# Revit family: VLGFP1002-xxxWSxxxBxxx
name_source: partatom
category: Oprawy oświetleniowe
revit_build: Autodesk Revit 2017 (Build: 20190508_0315(x64)
units: mm (PartAtom-declared; Revit-internal decimal feet)

## family parameters
Numer OmniClass = 23.80.70.11
Obiekt nadrzędny = Powierzchnia
Punkt obliczania pomieszczeń = Nie
Tnij formami wycięć po wczytaniu = Nie
Typ części = Normalny
Tytuł OmniClass = Luminaries for Internal Lighting
Współdzielony = Nie
Wymiar okrągłego złącza = Użyj średnicy
Źródło światła = Tak

## types (16) — shared parameters
Emituj kształt widoczny w renderingu = Nie
Emituj z długości prostokąta = 63 mm  [stored 0.206693 ft]
Emituj z szerokości prostokąta = 969 mm
Filtr koloru = 16777215
Kod zespołu = D5020200
Lampa = LED
Odchylenie kierunku = 90.00°
Plik sieci fotometrycznej = VLGFP1501-5NDWS840B0800.IES
Producent = RIDI Leuchten GmbH
URL = www.ridi.de
Zmiana temperatury barwowej przyciemniania lampy = <Brak>
brand = RIDI
conformity mark = CE
electrical safety class = 1
height = 66 mm  [stored 0.216535 ft]
ingress protection (IP) code = IP54
length = 1000 mm  [stored 3.28084 ft]
nominal frequency = 50-60Hz
nominal voltage = 230
voltage type (AC, DC, UC) = AC
weight = 1.64 kg
width = 67 mm
zero-valued in all types: Domyślna rzędna

## per-type parameters (varying)
| type | Model | Obciążenie pozorne | product name | rated input power |
| VLGFP1002-5NDWS830B0950 | 1551033 | 66 VA | VLGFP1002-5NDWS830B0950 | 66 |
| VLGFP1002-7DAWS830B0950 | 1561033
1561033
1561033 | 66 VA | VLGFP1002-7DAWS830B0950 | 66 |
| VLGFP1002-5NDWS830B1100 | 1551093 | 81 VA | VLGFP1002-5NDWS830B1100 | 81 |
| VLGFP1002-7DAWS830B1100 | 1561093 | 81 VA | VLGFP1002-5NDWS830B1100 | 81 |
| VLGFP1002-5NDWS840B1000 | 1551013 | 66 VA | VLGFP1002-5NDWS830B1100 | 66 |
| VLGFP1002-7DAWS840B1000 | 1561013 | 66 VA | VLGFP1002-7DAWS840B1000 | 66 |
| VLGFP1002-5NDWS840B1200 | 1551089 | 81 VA | VLGFP1002-5NDWS840B1200 | 81 |
| VLGFP1002-7NDWS840B1200 | 1561089 | 81 VA | VLGFP1002-7NDWS840B1200 | 81 |
| VLGFP1002-5NDWS850B1000 | 1551046 | 66 VA | VLGFP1002-5NDWS850B1000 | 66 |
| VLGFP1002-7DAWS850B1000 | 1561046 | 66 VA | VLGFP1002-7DAWS850B1000 | 66 |
| VLGFP1002-5NDWS850B1200 | 1551095 | 81 VA | VLGFP1002-5NDWS850B1200 | 81 |
| VLGFP1002-7DAWS850B1200 | 1561095 | 81 VA | VLGFP1002-7DAWS850B1200 | 81 |
| VLGFP1002-5NDWS865B1000 | 1551059 | 66 VA | VLGFP1002-5NDWS865B1000 | 66 |
| VLGFP1002-7DAWS865B1000 | 1561059 | 66 VA | VLGFP1002-7DAWS865B1000 | 66 |
| VLGFP1002-5NDWS865B1200 | 1551099 | 81 VA | VLGFP1002-5NDWS865B1200 | 81 |
| VLGFP1002-7DAWS865B1200 | 1561099 | 81 VA | VLGFP1002-7DAWS865B1200 | 81 |

note: [stored X ft] marks values corroborated as IEEE doubles in the binary element streams (Revit-internal decimal feet)
